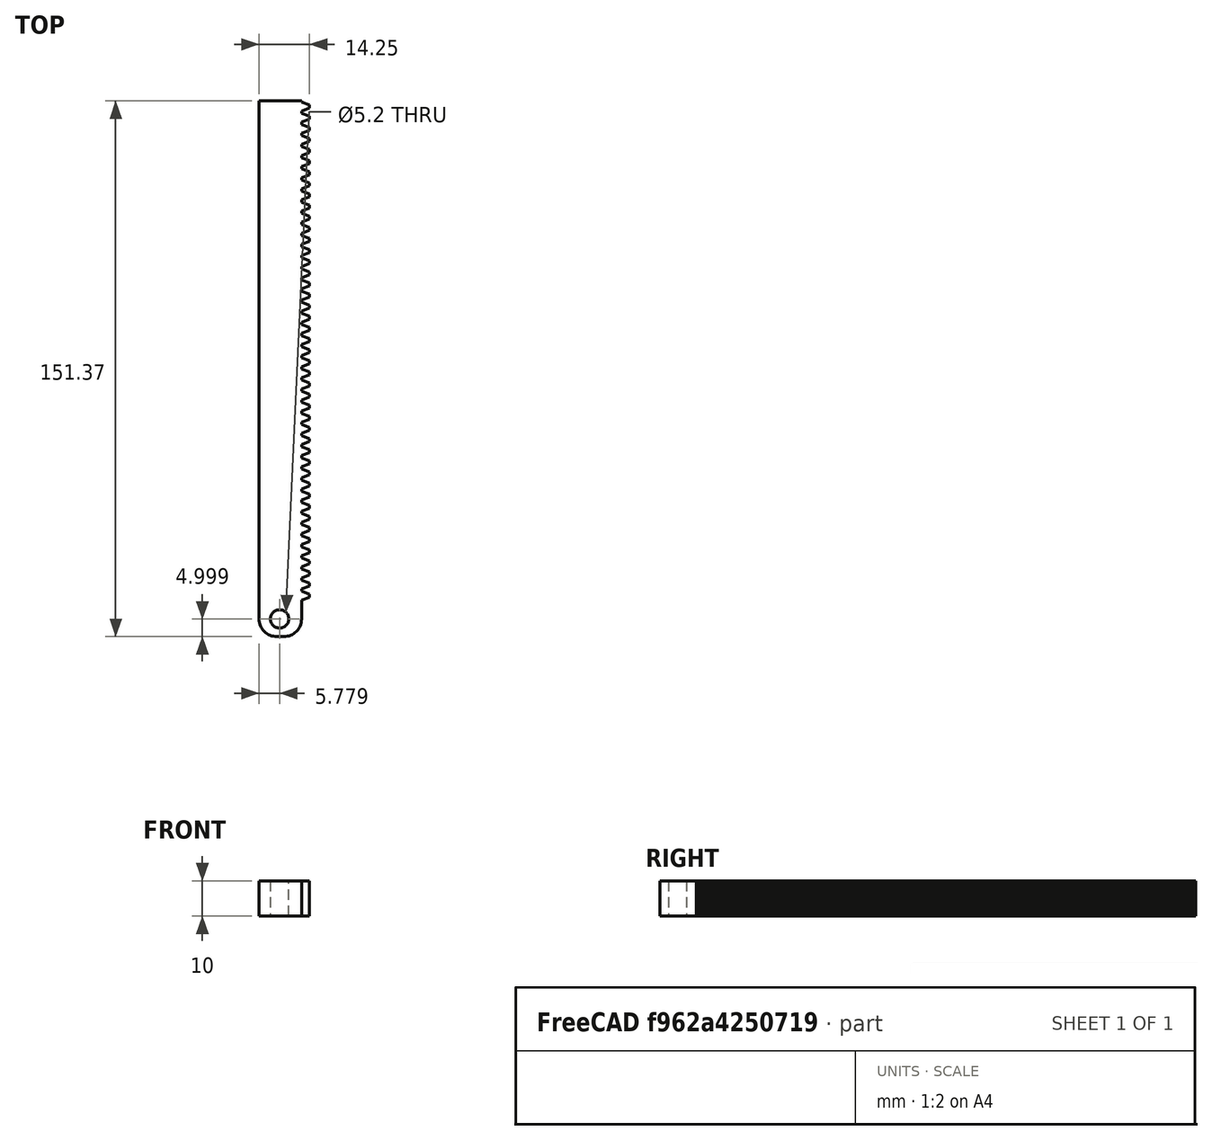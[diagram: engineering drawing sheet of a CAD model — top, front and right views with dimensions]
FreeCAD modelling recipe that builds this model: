
FCSTD DOCUMENT  (FreeCAD 0.20R29410 (Git))
Label: rack_v3
License: All rights reserved
LicenseURL: http://en.wikipedia.org/wiki/All_rights_reserved
objects: TechDraw::DrawViewDimension×11, TechDraw::DrawProjGroupItem×3, PartDesign::FeaturePython×1, PartDesign::Pad×1, Sketcher::SketchObject×1, PartDesign::Body×1, Part::Extrusion×1, Part::Cut×1, Part::Fillet×1, TechDraw::DrawSVGTemplate×1, TechDraw::DrawProjGroup×1, TechDraw::DrawPage×1
note: 8 computed .brp shape members not serialized (recipe doc carries the construction recipe); baked Part::Feature solids carry a one-line shape summary decoded from their .brp

FEATURE [PartDesign::FeaturePython] InvoluteRack  # WARN: FeaturePython — macro-defined, semantics opaque (R4)
  AttacherType = Attacher::AttachEngine3D
  add_endings = true
  beta = 0
  clearance = 0.25
  double_helix = false
  head = 0
  head_fillet = 0
  height = 10
  module = 1
  pressure_angle = 20
  properties_from_tool = false
  root_fillet = 0
  simplified = false
  teeth = 45
  thickness = 12
  transverse_pitch = 3.14159
  version = 0.0.4
FEATURE [PartDesign::Pad] Pad
  BaseFeature = -> InvoluteRack
  Direction = (0,-1,0)
  Length = 10
  Length2 = 10
  Profile = -> InvoluteRack [Face1]
  Type = 0
FEATURE [Sketcher::SketchObject] Sketch
  FullyConstrained = false
  MapMode = 5
  Placement = pos=(0,0,10) rot=(0,0,1;0rad)
  Support = -> [Pad]
  sketch-geometry (1):
    g0: Circle CenterX=-7.47114 CenterY=-6.5708 CenterZ=0 NormalX=0 NormalY=0 NormalZ=1 AngleXU=0 Radius=2.6
  constraints (1):
    c: Diameter(g0) = 5.2
FEATURE [PartDesign::Body] Body
  Group = -> [InvoluteRack,Pad,Sketch]
  Origin = -> Origin
  Tip = -> Pad
FEATURE [Part::Extrusion] Extrude
  Base = -> Sketch
  Dir = (0,0,1)
  DirMode = 2
  FaceMakerClass = Part::FaceMakerBullseye
  LengthFwd = 10
  LengthRev = 20
  Solid = true
  Symmetric = false
FEATURE [Part::Cut] Cut
  Base = -> Body
  Tool = -> Extrude
FEATURE [Part::Fillet] Fillet
  Base = -> Cut
  Edges = 2 edges r=5: [Edge7,Edge381]
FEATURE [TechDraw::DrawSVGTemplate] Template
  EditableTexts = Designed_by_Name=Белкин Никита; FC-Date=24.04.2023; FC-SC=1:2; FC-Title=Зубчатая рейка
  Height = 210
  Orientation = 1
  Width = 297
FEATURE [TechDraw::DrawProjGroupItem] ProjItem  label="Front"
  CoarseView = false
  Direction = (0,1,0)
  Focus = 100
  HardHidden = false
  IsoCount = 0
  IsoHidden = false
  IsoVisible = false
  LockPosition = true
  Perspective = false
  Rotation = 0
  RotationVector = (0,0,1)
  ScaleType = 2
  SeamHidden = false
  SeamVisible = true
  SmoothHidden = false
  SmoothVisible = true
  Source = -> [Fillet]
  Type = 0
  X = 0
  XDirection = (0,0,1)
  Y = 0
FEATURE [TechDraw::DrawProjGroupItem] ProjItem001  label="Top"
  CoarseView = false
  Direction = (1,0,0)
  Focus = 100
  HardHidden = false
  IsoCount = 0
  IsoHidden = false
  IsoVisible = false
  LockPosition = false
  Perspective = false
  Rotation = 0
  RotationVector = (1,0,0)
  ScaleType = 2
  SeamHidden = false
  SeamVisible = true
  SmoothHidden = false
  SmoothVisible = true
  Source = -> [Fillet]
  Type = 4
  X = 0
  XDirection = (0,0,1)
  Y = -89.6962
FEATURE [TechDraw::DrawProjGroupItem] ProjItem002  label="Left"
  CoarseView = false
  Direction = (0,1e-16,-1)
  Focus = 100
  HardHidden = false
  IsoCount = 0
  IsoHidden = false
  IsoVisible = false
  LockPosition = false
  Perspective = false
  Rotation = 0
  RotationVector = (1,0,0)
  ScaleType = 2
  SeamHidden = false
  SeamVisible = true
  SmoothHidden = false
  SmoothVisible = true
  Source = -> [Fillet]
  Type = 1
  X = 98.3438
  XDirection = (0,1,1e-16)
  Y = 0
FEATURE [TechDraw::DrawProjGroup] ProjGroup
  Anchor = -> ProjItem
  AutoDistribute = true
  LockPosition = false
  ProjectionType = 0
  Rotation = 0
  ScaleType = 0
  Source = -> [Fillet]
  Views = -> [ProjItem,ProjItem001,ProjItem002]
  X = 62.59
  Y = 179.446
  spacingX = 15
  spacingY = 15
FEATURE [TechDraw::DrawViewDimension] Dimension
  AngleOverride = false
  Arbitrary = false
  ArbitraryTolerances = false
  EqualTolerance = true
  ExtensionAngle = 0
  FormatSpec = %.2w
  FormatSpecOverTolerance = %+.2w
  FormatSpecUnderTolerance = %+.2w
  Inverted = false
  LineAngle = 0
  LockPosition = false
  MeasureType = 1
  OverTolerance = 0
  References2D = -> [ProjItem]
  Rotation = 0
  ScaleType = 0
  TheoreticalExact = false
  Type = 1
  UnderTolerance = 0
  X = -1.41374
  Y = 19.1835
FEATURE [TechDraw::DrawViewDimension] Dimension001
  AngleOverride = false
  Arbitrary = false
  ArbitraryTolerances = false
  EqualTolerance = true
  ExtensionAngle = 0
  FormatSpec = %.2w
  FormatSpecOverTolerance = %+.2w
  FormatSpecUnderTolerance = %+.2w
  Inverted = false
  LineAngle = 0
  LockPosition = false
  MeasureType = 1
  OverTolerance = 0
  References2D = -> [ProjItem]
  Rotation = 0
  ScaleType = 0
  TheoreticalExact = false
  Type = 2
  UnderTolerance = 0
  X = -20.1355
  Y = 14.4472
FEATURE [TechDraw::DrawViewDimension] Dimension002
  AngleOverride = false
  Arbitrary = false
  ArbitraryTolerances = false
  EqualTolerance = true
  ExtensionAngle = 0
  FormatSpec = %.2w
  FormatSpecOverTolerance = %+.2w
  FormatSpecUnderTolerance = %+.2w
  Inverted = false
  LineAngle = 0
  LockPosition = false
  MeasureType = 1
  OverTolerance = 0
  References2D = -> [ProjItem]
  Rotation = 0
  ScaleType = 0
  TheoreticalExact = false
  Type = 2
  UnderTolerance = 0
  X = -28.6237
  Y = -9.44958
FEATURE [TechDraw::DrawViewDimension] Dimension003
  AngleOverride = false
  Arbitrary = false
  ArbitraryTolerances = false
  EqualTolerance = true
  ExtensionAngle = 0
  FormatSpec = R%.2w
  FormatSpecOverTolerance = %+.2w
  FormatSpecUnderTolerance = %+.2w
  Inverted = false
  LineAngle = 0
  LockPosition = false
  MeasureType = 1
  OverTolerance = 0
  References2D = -> [ProjItem002]
  Rotation = 0
  ScaleType = 0
  TheoreticalExact = false
  Type = 4
  UnderTolerance = 0
  X = -53.5045
  Y = -17.4763
FEATURE [TechDraw::DrawViewDimension] Dimension004
  AngleOverride = false
  Arbitrary = false
  ArbitraryTolerances = false
  EqualTolerance = true
  ExtensionAngle = 0
  FormatSpec = ⌀%.2w
  FormatSpecOverTolerance = %+.2w
  FormatSpecUnderTolerance = %+.2w
  Inverted = false
  LineAngle = 0
  LockPosition = false
  MeasureType = 1
  OverTolerance = 0
  References2D = -> [ProjItem002]
  Rotation = 0
  ScaleType = 0
  TheoreticalExact = false
  Type = 5
  UnderTolerance = 0
  X = -47.7239
  Y = -9.54477
FEATURE [TechDraw::DrawViewDimension] Dimension005
  AngleOverride = false
  Arbitrary = false
  ArbitraryTolerances = false
  EqualTolerance = true
  ExtensionAngle = 0
  FormatSpec = %.2w
  FormatSpecOverTolerance = %+.2w
  FormatSpecUnderTolerance = %+.2w
  Inverted = false
  LineAngle = 0
  LockPosition = false
  MeasureType = 1
  OverTolerance = 0
  References2D = -> [ProjItem002]
  Rotation = 0
  ScaleType = 0
  TheoreticalExact = false
  Type = 1
  UnderTolerance = 0
  X = 82.4291
  Y = -5.25131
FEATURE [TechDraw::DrawViewDimension] Dimension006
  AngleOverride = false
  Arbitrary = false
  ArbitraryTolerances = false
  EqualTolerance = true
  ExtensionAngle = 0
  FormatSpec = %.2w
  FormatSpecOverTolerance = %+.2w
  FormatSpecUnderTolerance = %+.2w
  Inverted = false
  LineAngle = 0
  LockPosition = false
  MeasureType = 1
  OverTolerance = 0
  References2D = -> [ProjItem002]
  Rotation = 0
  ScaleType = 0
  TheoreticalExact = false
  Type = 1
  UnderTolerance = 0
  X = 67.2047
  Y = -14.2819
FEATURE [TechDraw::DrawViewDimension] Dimension007
  AngleOverride = false
  Arbitrary = false
  ArbitraryTolerances = false
  EqualTolerance = true
  ExtensionAngle = 0
  FormatSpec = %.2w
  FormatSpecOverTolerance = %+.2w
  FormatSpecUnderTolerance = %+.2w
  Inverted = false
  LineAngle = 0
  LockPosition = false
  MeasureType = 1
  OverTolerance = 0
  References2D = -> [ProjItem002]
  Rotation = 0
  ScaleType = 0
  TheoreticalExact = false
  Type = 1
  UnderTolerance = 0
  X = 37.3487
  Y = -8.18778
FEATURE [TechDraw::DrawViewDimension] Dimension008
  AngleOverride = false
  Arbitrary = false
  ArbitraryTolerances = false
  EqualTolerance = true
  ExtensionAngle = 0
  FormatSpec = %.2w
  FormatSpecOverTolerance = %+.2w
  FormatSpecUnderTolerance = %+.2w
  Inverted = false
  LineAngle = 0
  LockPosition = false
  MeasureType = 1
  OverTolerance = 0
  References2D = -> [ProjItem001]
  Rotation = 0
  ScaleType = 0
  TheoreticalExact = false
  Type = 2
  UnderTolerance = 0
  X = -23.9788
  Y = 3.46805
FEATURE [TechDraw::DrawViewDimension] Dimension009
  AngleOverride = false
  Arbitrary = false
  ArbitraryTolerances = false
  EqualTolerance = true
  ExtensionAngle = 0
  FormatSpec = %.2w
  FormatSpecOverTolerance = %+.2w
  FormatSpecUnderTolerance = %+.2w
  Inverted = false
  LineAngle = 0
  LockPosition = false
  MeasureType = 1
  OverTolerance = 0
  References2D = -> [ProjItem001]
  Rotation = 0
  ScaleType = 0
  TheoreticalExact = false
  Type = 2
  UnderTolerance = 0
  X = 9.85028
  Y = 67.3806
FEATURE [TechDraw::DrawViewDimension] Dimension010
  AngleOverride = false
  Arbitrary = false
  ArbitraryTolerances = false
  EqualTolerance = true
  ExtensionAngle = 0
  FormatSpec = %.2w
  FormatSpecOverTolerance = %+.2w
  FormatSpecUnderTolerance = %+.2w
  Inverted = false
  LineAngle = 0
  LockPosition = false
  MeasureType = 1
  OverTolerance = 0
  References2D = -> [ProjItem001]
  Rotation = 0
  ScaleType = 0
  TheoreticalExact = false
  Type = 2
  UnderTolerance = 0
  X = -13.2446
  Y = 64.2852
FEATURE [TechDraw::DrawPage] Page
  KeepUpdated = true
  NextBalloonIndex = 1
  ProjectionType = 0
  Template = -> Template
  Views = -> [ProjGroup,Dimension,Dimension001,Dimension002,Dimension003,Dimension004,Dimension005,Dimension006,Dimension007,Dimension008,Dimension009,Dimension010]
